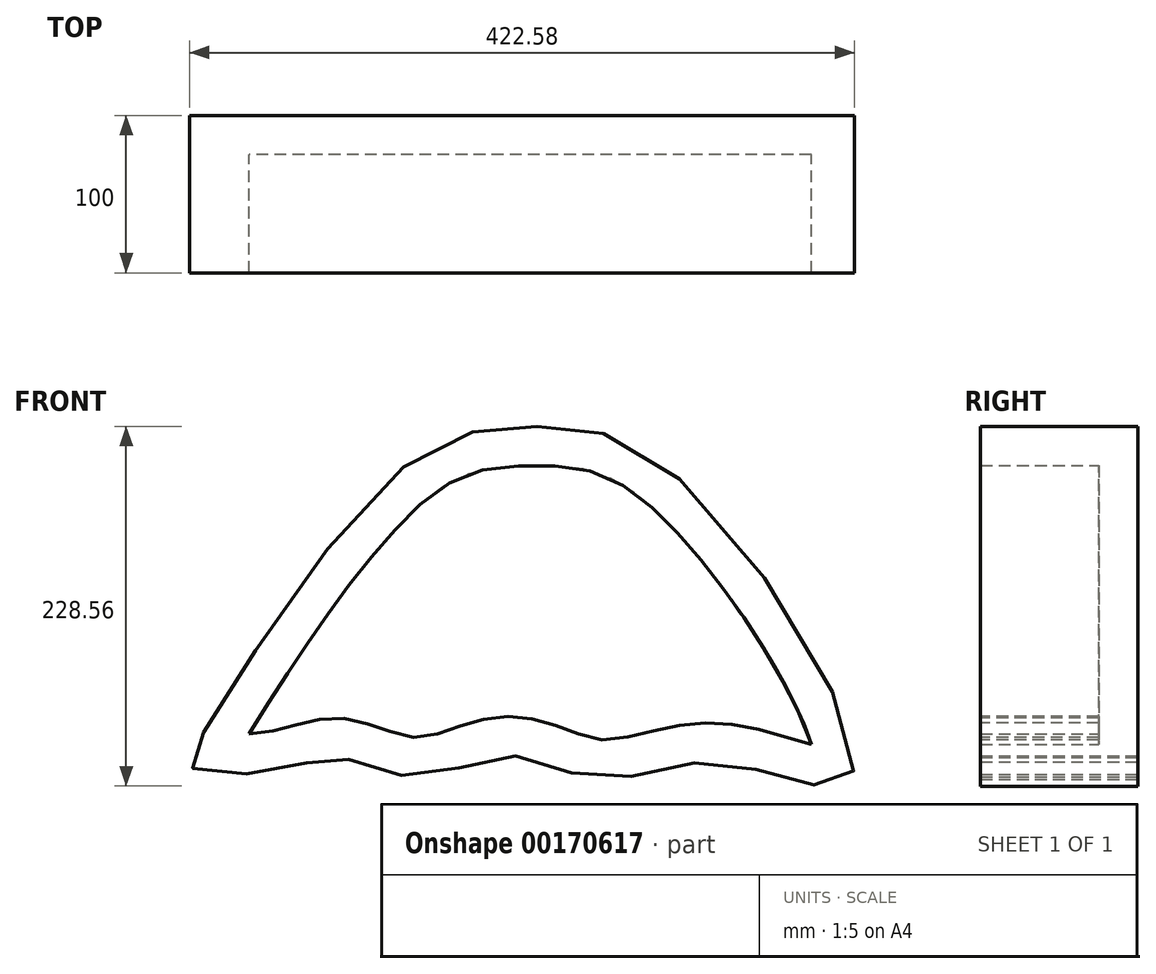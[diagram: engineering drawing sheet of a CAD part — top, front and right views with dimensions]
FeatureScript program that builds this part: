
annotation { "Feature Type Name" : "Feature", "Feature Type Description" : "" }
export const myFeature = defineFeature(function(context is Context, id is Id, definition is map)
    precondition{}
    {
        {
            var Q0;
            Q0=qCreatedBy(makeId("Front.planeOp"),FACE);
            var sketch = newSketch(context, id + "F0", { "sketchPlane" : qUnion([Q0])});
            skFitSpline(sketch, "E0", {"points": [v(-227.64, -45.9) * mm, v(-234.35, -68.69) * mm, v(-175.35, -68.69) * mm, v(-140.48, -61.98) * mm, v(-90.87, -74.05) * mm, v(-33.2, -60.64) * mm, v(23.11, -75.4) * mm, v(91.5, -64.66) * mm, v(154.52, -78.07) * mm, v(185.36, -70.03) * mm, v(70.04, 119.04) * mm, v(-19.8, 148.54) * mm, v(-100.25, 123.07) * mm, v(-227.64, -45.9) * mm]});
            skSolve(sketch);
        }
        {
            var Q0;
            Q0 = qSketchRegion(id + "F0", true);
            extrude(context, id + "F1", {"entities" : qUnion([Q0]), "depth" : 100 * mm});
        }
        {
            var Q0;
            Q0=makeQuery(id+"F1.opExtrude","CAP_FACE",FACE,{"disambiguationData":[OSD([sQuery(id+"F0.wireOp",EDGE,"E0")])],"isStart":false});
            shell(context, id + "F2", {"entities" : qUnion([Q0]), "thickness" : 25 * mm});
        }
    });
